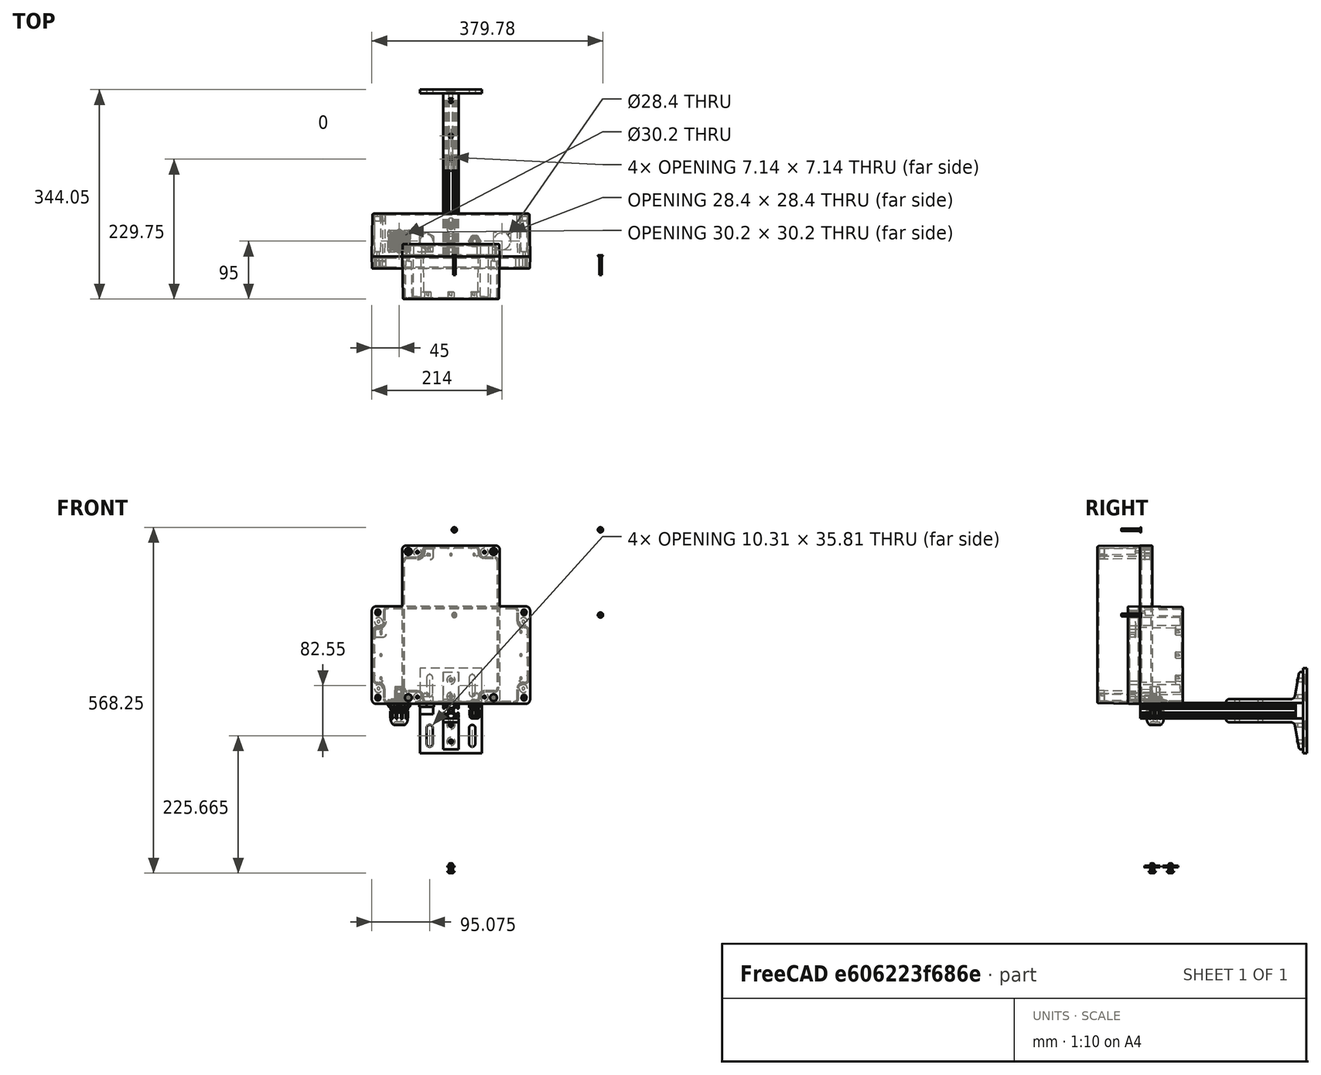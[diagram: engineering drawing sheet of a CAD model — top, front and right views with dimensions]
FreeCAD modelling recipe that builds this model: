
FCSTD DOCUMENT  (FreeCAD 0.20R29410 (Git))
Label: gateWayModuleTest
License: All rights reserved
LicenseURL: http://en.wikipedia.org/wiki/All_rights_reserved
objects: Part::Feature×42, TechDraw::DrawViewDimension×36, Part::Cylinder×28, Part::MultiFuse×9, App::Part×8, Part::Cut×4, TechDraw::DrawViewPart×4, TechDraw::DrawSVGTemplate×2, TechDraw::DrawPage×2, Part::Box×1, Sketcher::SketchObject×1, Part::Extrusion×1, TechDraw::DrawViewAnnotation×1
note: 86 computed .brp shape members not serialized (recipe doc carries the construction recipe); baked Part::Feature solids carry a one-line shape summary decoded from their .brp

FEATURE [Part::Feature] Part__Feature  label="AN-23B_AN-23BP-01"
  shape: bbox 160 x 71.5 x 260 mm, 302 faces (baked)
FEATURE [Part::Feature] Part__Feature001  label="AN-23C_AN-23C-01"
  shape: bbox 160.5 x 20 x 260.5 mm, 243 faces (baked)
FEATURE [Part::Feature] Part__Feature002  label="cross recessed countersunk head screw_jis_JIS 1111 Cross recessed countersunk head screw - M4 x 32 - Z --24CSST"
  Placement = pos=(245.578,1.4369,155.7) rot=(0.642635,-0.642635,0.417181;3.93205rad)
  shape: bbox 8.4 x 32 x 8.4 mm, 32 faces (baked)
FEATURE [Part::Feature] Part__Feature003  label="cross recessed countersunk head screw_jis_JIS 1111 Cross recessed countersunk head screw - M4 x 32 - Z --24CSST001"
  Placement = pos=(245.578,1.4369,15.6996) rot=(0.610522,-0.610522,0.504506;4.07608rad)
  shape: bbox 8.4 x 32 x 8.4 mm, 32 faces (baked)
FEATURE [Part::Feature] Part__Feature004  label="cross recessed countersunk head screw_jis_JIS 1111 Cross recessed countersunk head screw - M4 x 32 - Z --24CSST002"
  Placement = pos=(5.5776,1.4369,15.6996) rot=(0.641113,-0.641113,0.421839;3.93997rad)
  shape: bbox 8.4 x 32 x 8.4 mm, 32 faces (baked)
FEATURE [Part::Feature] Part__Feature005  label="cross recessed countersunk head screw_jis_JIS 1111 Cross recessed countersunk head screw - M4 x 32 - Z --24CSST003"
  Placement = pos=(5.5776,1.4369,155.7) rot=(0.666667,-0.666667,0.333333;3.78509rad)
  shape: bbox 8.4 x 32 x 8.4 mm, 32 faces (baked)
FEATURE [App::Part] SCREWS_036_4  label="SCREWS-036-4"
  Group = -> [Part__Feature002,Part__Feature003,Part__Feature004,Part__Feature005]
  Origin = -> Origin
  Placement = pos=(85.6996,18.1356,-125.578) rot=(0,-1,0;1.5708rad)
FEATURE [Part::Feature] Part__Feature006  label="GASKET-123-01"
  Placement = pos=(0,1.04,0) rot=(0,0,1;0rad)
  shape: bbox 157.7 x 1.5 x 257.7 mm, 98 faces (baked)
FEATURE [App::Part] AN_23P_01  label="AN-23P-01"
  Group = -> [Part__Feature,Part__Feature001,SCREWS_036_4,Part__Feature006]
  Origin = -> Origin001
  Placement = pos=(0,0,-50) rot=(0.707107,0,-0.707107;3.14159rad)
FEATURE [Part::Box] Box  label="Gateway"
  AttacherType = Attacher::AttachEngine3D
  Height = 120
  Length = 120
  Placement = pos=(-66,26,-100) rot=(0,0,1;0rad)
  Width = 30
FEATURE [Part::Cylinder] Cylinder030  label="loraAntenna"
  Angle = 360
  AttacherType = Attacher::AttachEngine3D
  FirstAngle = 0
  Height = 1390
  Radius = 13
  SecondAngle = 0
FEATURE [Part::Cylinder] Cylinder031  label="loraAntenna001"
  Angle = 360
  AttacherType = Attacher::AttachEngine3D
  FirstAngle = 0
  Height = 204
  Radius = 15
  SecondAngle = 0
FEATURE [Part::Cylinder] Cylinder032  label="loraAntenna002"
  Angle = 360
  AttacherType = Attacher::AttachEngine3D
  FirstAngle = 0
  Height = 27
  Placement = pos=(0,0,1363) rot=(0,0,1;0rad)
  Radius = 14
  SecondAngle = 0
FEATURE [Part::MultiFuse] Fusion006  label="loraAntenna003"
  Placement = pos=(0,0,188) rot=(0,0,1;0rad)
  Shapes = -> [Cylinder030,Cylinder032]
FEATURE [Part::MultiFuse] Fusion007  label="loraAntenna004"
  Placement = pos=(0,103,-127) rot=(0,0,1;0rad)
  Shapes = -> [Fusion006,Cylinder031]
FEATURE [Part::Feature] Part__Feature008  label="CUI_VGS-25W-5"
  Placement = pos=(-42,23,-27) rot=(1,0,0;3.14159rad)
  shape: bbox 55.36 x 25.53 x 90.37 mm, 2734 faces, 26 solids (baked)
FEATURE [Part::Feature] Part__Feature009  label="DCC-RJ6ST-310"
  Placement = pos=(-85,25,-123) rot=(0,0,1;0rad)
  shape: bbox 40.36 x 68.07 x 51.72 mm, 441 faces (baked)
FEATURE [Part::Feature] Part__Feature010  label="DCP-RJ6ST-F"
  Placement = pos=(-85,25,-123.5) rot=(0,1,0;3.14159rad)
  shape: bbox 40.26 x 40.33 x 38.85 mm, 485 faces, 2 solids (baked)
FEATURE [Part::Cylinder] Cylinder  label="plugIn"
  Angle = 360
  AttacherType = Attacher::AttachEngine3D
  FirstAngle = 0
  Height = 28.19
  Radius = 11
  SecondAngle = 0
FEATURE [Sketcher::SketchObject] Sketch
  FullyConstrained = true
  sketch-geometry (7):
    g0: LineSegment StartX=12.25 StartY=-7.07254 StartZ=0 EndX=12.25 EndY=7.07254 EndZ=0
    g1: LineSegment StartX=12.25 StartY=7.07254 StartZ=0 EndX=0 EndY=14.1451 EndZ=0
    g2: LineSegment StartX=0 StartY=14.1451 StartZ=0 EndX=-12.25 EndY=7.07254 EndZ=0
    g3: LineSegment StartX=-12.25 StartY=7.07254 StartZ=0 EndX=-12.25 EndY=-7.07254 EndZ=0
    g4: LineSegment StartX=-12.25 StartY=-7.07254 StartZ=0 EndX=0 EndY=-14.1451 EndZ=0
    g5: LineSegment StartX=0 StartY=-14.1451 StartZ=0 EndX=12.25 EndY=-7.07254 EndZ=0
    g6: Circle CenterX=0 CenterY=0 CenterZ=0 NormalX=0 NormalY=0 NormalZ=1 AngleXU=0 Radius=14.1451
  constraints (17):
    c: Coincident(g0,g1)
    c: Coincident(g1,g2)
    c: Coincident(g2,g3)
    c: Coincident(g3,g4)
    c: Coincident(g4,g5)
    c: Coincident(g5,g0)
    c: Equal(g0, g1-g5) x5
    c: PointOnObject(g0,g6)
    c: PointOnObject(g1,g6)
    c: PointOnObject(g2,g6)
    c: PointOnObject(g3,g6)
    c: PointOnObject(g4,g6)
    c: PointOnObject(g5,g6)
    c: DistanceY(g6) = 0
    c: DistanceX(g6) = 0
    c: DistanceX(g1) = 0
    c: DistanceX(g2,g0) = 24.5
FEATURE [Part::Extrusion] Extrude
  Base = -> Sketch
  Dir = (0,0,1)
  DirMode = 2
  FaceMakerClass = Part::FaceMakerBullseye
  LengthFwd = 4.83
  LengthRev = 0
  Placement = pos=(0,0,12.19) rot=(0,0,1;0rad)
  Solid = true
  Symmetric = false
FEATURE [Part::MultiFuse] Fusion  label="powerPlug"
  Placement = pos=(-40,25,-147) rot=(0,0,1;0rad)
  Shapes = -> [Cylinder,Extrude]
FEATURE [Part::Feature] Part__Feature021  label="LoRaAntennaGland"
  Placement = pos=(84,25,-120) rot=(-1,0,0;1.5708rad)
  shape: bbox 36.99 x 36.69 x 48.04 mm, 518 faces, 0 solids (baked)
FEATURE [Part::Feature] Part__Feature022  label="3136N138_T-Slotted Framing"
  Placement = pos=(0,200.3,0) rot=(0,0,1;0rad)
  shape: bbox 101.6 x 133.4 x 139.7 mm, 136 faces (baked)
FEATURE [Part::Feature] Part__Feature023  label="47065T801_T-Slotted Framing"
  Placement = pos=(0,288.5,0) rot=(-1,0,0;1.5708rad)
  shape: bbox 25.4 x 152.4 x 25.4 mm, 108 faces (baked)
FEATURE [Part::Feature] Part__Feature024  label="47065T801_T-Slotted Framing001"
  Placement = pos=(0,391.5,0) rot=(-1,0,0;1.5708rad)
  shape: bbox 25.4 x 152.4 x 25.4 mm, 108 faces (baked)
FEATURE [Part::MultiFuse] Fusion008  label="framingSupport"
  Placement = pos=(0,468,-141.41) rot=(0,0,1;3.14159rad)
  Shapes = -> [Part__Feature024,Part__Feature022,Part__Feature023]
FEATURE [Part::Feature] Part__Feature025  label="Cable Gland PG7-PG19 Body_PG008"
  shape: bbox 17.67 x 27.9 x 16 mm, 147 faces (baked)
FEATURE [Part::Feature] Part__Feature026  label="Cable Gland PG7-PG19 Washer_PG008"
  Placement = pos=(0,-2.8,0) rot=(0,0,1;0rad)
  shape: bbox 16.6 x 1.2 x 16.6 mm, 6 faces (baked)
FEATURE [Part::Feature] Part__Feature027  label="Cable Gland PG7-PG19 Lock Nut_PG008"
  Placement = pos=(0,-5.6,0) rot=(0,0,1;3.14159rad)
  shape: bbox 19.6 x 5.77 x 19.6 mm, 32 faces (baked)
FEATURE [Part::Feature] Part__Feature028  label="Cable Gland PG7-PG19 Sleeve_PG008"
  Placement = pos=(0,13.65,0) rot=(0,0,1;0rad)
  shape: bbox 8.4 x 6.7 x 8.4 mm, 6 faces (baked)
FEATURE [Part::Feature] Part__Feature029  label="Cable Gland PG7-PG19 Gland Nut_PG008"
  Placement = pos=(0,10.95,0) rot=(0,-1,0;1.94172rad)
  shape: bbox 16.87 x 14 x 16.87 mm, 64 faces (baked)
FEATURE [Part::MultiFuse] Fusion011  label="pg7-Copper"
  Placement = pos=(39,25,-134) rot=(-1,0,0;1.5708rad)
  Shapes = -> [Part__Feature025,Part__Feature026,Part__Feature027,Part__Feature028,Part__Feature029]
FEATURE [Part::Cylinder] Cylinder033  label="EthernetCut"
  Angle = 360
  AttacherType = Attacher::AttachEngine3D
  FirstAngle = 0
  Height = 50
  Placement = pos=(-85,25,-147) rot=(0,0,1;0rad)
  Radius = 15.1
  SecondAngle = 0
FEATURE [Part::Cylinder] Cylinder034  label="PowerCut"
  Angle = 360
  AttacherType = Attacher::AttachEngine3D
  FirstAngle = 0
  Height = 50
  Placement = pos=(-40,25,-147) rot=(0,0,1;0rad)
  Radius = 11
  SecondAngle = 0
FEATURE [Part::Cylinder] Cylinder035  label="pg7Cut"
  Angle = 360
  AttacherType = Attacher::AttachEngine3D
  FirstAngle = 0
  Height = 50
  Placement = pos=(39,25,-147) rot=(0,0,1;0rad)
  Radius = 6.4
  SecondAngle = 0
FEATURE [Part::Cylinder] Cylinder036  label="AnetnnaCut"
  Angle = 360
  AttacherType = Attacher::AttachEngine3D
  FirstAngle = 0
  Height = 50
  Placement = pos=(84,25,-147) rot=(0,0,1;0rad)
  Radius = 14.2
  SecondAngle = 0
FEATURE [Part::Feature] Part__Feature030  label="47065T139_T-Slotted Framing"
  Placement = pos=(0,20,-405) rot=(0.57735,0.57735,-0.57735;4.18879rad)
  shape: bbox 11.25 x 25.4 x 17.44 mm, 56 faces, 2 solids (baked)
FEATURE [Part::Feature] Part__Feature031  label="47065T139_T-Slotted Framing001"
  Placement = pos=(0,50,-405) rot=(0.57735,0.57735,-0.57735;4.18879rad)
  shape: bbox 11.25 x 25.4 x 17.44 mm, 56 faces, 2 solids (baked)
FEATURE [Part::Cylinder] Cylinder037  label="m5Cut"
  Angle = 360
  AttacherType = Attacher::AttachEngine3D
  FirstAngle = 0
  Height = 50
  Placement = pos=(0,20,-147) rot=(0,0,1;0rad)
  Radius = 3.2
  SecondAngle = 0
FEATURE [Part::Cylinder] Cylinder038  label="m5Cut001"
  Angle = 360
  AttacherType = Attacher::AttachEngine3D
  FirstAngle = 0
  Height = 50
  Placement = pos=(0,50,-147) rot=(0,0,1;0rad)
  Radius = 3.2
  SecondAngle = 0
FEATURE [Part::MultiFuse] Fusion012
  Shapes = -> [Cylinder038,Cylinder037,Cylinder036,Cylinder035,Cylinder033,Cylinder034]
FEATURE [Part::Cut] Cut
  Base = -> AN_23P_01
  Tool = -> Fusion012
FEATURE [TechDraw::DrawSVGTemplate] Template
  EditableTexts = Designed_by_Name=Lakitha Wijeratne; Drawing_number=V1; FC-Date=November 14th 2022; FC-SC=0.5; FC-Title=MINTS Gateway Module; Subtitle=Cutouts for Polycase AN-23P Black
  Height = 210
  Orientation = 1
  Width = 297
FEATURE [TechDraw::DrawViewPart] View  label="Internal View"
  CoarseView = false
  Direction = (0.577,-0.577,0.577)
  Focus = 100
  HardHidden = false
  IsoCount = 0
  IsoHidden = false
  IsoVisible = false
  LockPosition = false
  Perspective = false
  Rotation = 0
  Scale = 0.5
  ScaleType = 0
  SeamHidden = false
  SeamVisible = true
  SmoothHidden = false
  SmoothVisible = true
  Source = -> [Cut]
  X = 221.274
  XDirection = (0.707,0.707,0)
  Y = 135.96
FEATURE [TechDraw::DrawViewPart] View001  label="Bottom View"
  CoarseView = false
  Direction = (0,0,-1)
  Focus = 100
  HardHidden = false
  IsoCount = 0
  IsoHidden = false
  IsoVisible = false
  LockPosition = false
  Perspective = false
  Rotation = 0
  Scale = 0.5
  ScaleType = 0
  SeamHidden = false
  SeamVisible = true
  SmoothHidden = false
  SmoothVisible = true
  Source = -> [Cut]
  X = 84.2092
  XDirection = (1,0,0)
  Y = 168.275
FEATURE [Part::Cylinder] Cylinder039  label="EthernetCut001"
  Angle = 360
  AttacherType = Attacher::AttachEngine3D
  FirstAngle = 0
  Height = 50
  Placement = pos=(-85,25,-147) rot=(0,0,1;0rad)
  Radius = 15.1
  SecondAngle = 0
FEATURE [Part::Cylinder] Cylinder040  label="PowerCut001"
  Angle = 360
  AttacherType = Attacher::AttachEngine3D
  FirstAngle = 0
  Height = 50
  Placement = pos=(-40,25,-147) rot=(0,0,1;0rad)
  Radius = 11
  SecondAngle = 0
FEATURE [Part::Cylinder] Cylinder041  label="pg7Cut001"
  Angle = 360
  AttacherType = Attacher::AttachEngine3D
  FirstAngle = 0
  Height = 50
  Placement = pos=(39,25,-147) rot=(0,0,1;0rad)
  Radius = 6.4
  SecondAngle = 0
FEATURE [Part::Cylinder] Cylinder042  label="AnetnnaCut001"
  Angle = 360
  AttacherType = Attacher::AttachEngine3D
  FirstAngle = 0
  Height = 50
  Placement = pos=(84,25,-147) rot=(0,0,1;0rad)
  Radius = 14.2
  SecondAngle = 0
FEATURE [Part::Cylinder] Cylinder043  label="m5Cut002"
  Angle = 360
  AttacherType = Attacher::AttachEngine3D
  FirstAngle = 0
  Height = 50
  Placement = pos=(0,20,-147) rot=(0,0,1;0rad)
  Radius = 3.2
  SecondAngle = 0
FEATURE [Part::Cylinder] Cylinder044  label="m5Cut003"
  Angle = 360
  AttacherType = Attacher::AttachEngine3D
  FirstAngle = 0
  Height = 50
  Placement = pos=(0,50,-147) rot=(0,0,1;0rad)
  Radius = 3.2
  SecondAngle = 0
FEATURE [Part::MultiFuse] Fusion013
  Shapes = -> [Cylinder044,Cylinder043,Cylinder042,Cylinder041,Cylinder039,Cylinder040]
FEATURE [Part::Feature] Part__Feature032  label="AN-23B_AN-23BP-002"
  shape: bbox 160 x 71.5 x 260 mm, 302 faces (baked)
FEATURE [Part::Feature] Part__Feature033  label="AN-23C_AN-23C-002"
  shape: bbox 160.5 x 20 x 260.5 mm, 243 faces (baked)
FEATURE [Part::Feature] Part__Feature034  label="cross recessed countersunk head screw_jis_JIS 1111 Cross recessed countersunk head screw - M4 x 32 - Z --24CSST004"
  Placement = pos=(245.578,1.4369,155.7) rot=(0.642635,-0.642635,0.417181;3.93205rad)
  shape: bbox 8.4 x 32 x 8.4 mm, 32 faces (baked)
FEATURE [Part::Feature] Part__Feature035  label="cross recessed countersunk head screw_jis_JIS 1111 Cross recessed countersunk head screw - M4 x 32 - Z --24CSST005"
  Placement = pos=(245.578,1.4369,15.6996) rot=(0.610522,-0.610522,0.504506;4.07608rad)
  shape: bbox 8.4 x 32 x 8.4 mm, 32 faces (baked)
FEATURE [Part::Feature] Part__Feature036  label="cross recessed countersunk head screw_jis_JIS 1111 Cross recessed countersunk head screw - M4 x 32 - Z --24CSST006"
  Placement = pos=(5.5776,1.4369,15.6996) rot=(0.641113,-0.641113,0.421839;3.93997rad)
  shape: bbox 8.4 x 32 x 8.4 mm, 32 faces (baked)
FEATURE [Part::Feature] Part__Feature037  label="cross recessed countersunk head screw_jis_JIS 1111 Cross recessed countersunk head screw - M4 x 32 - Z --24CSST007"
  Placement = pos=(5.5776,1.4369,155.7) rot=(0.666667,-0.666667,0.333333;3.78509rad)
  shape: bbox 8.4 x 32 x 8.4 mm, 32 faces (baked)
FEATURE [Part::Feature] Part__Feature038  label="GASKET-123-002"
  Placement = pos=(0,1.04,0) rot=(0,0,1;0rad)
  shape: bbox 157.7 x 1.5 x 257.7 mm, 98 faces (baked)
FEATURE [App::Part] SCREWS_036_005  label="SCREWS-036-005"
  Group = -> [Part__Feature034,Part__Feature035,Part__Feature036,Part__Feature037]
  Origin = -> Origin002
  Placement = pos=(85.6996,18.1356,-125.578) rot=(0,-1,0;1.5708rad)
FEATURE [App::Part] AN_23P_002  label="AN-23P-002"
  Group = -> [Part__Feature032,Part__Feature033,SCREWS_036_005,Part__Feature038]
  Origin = -> Origin003
  Placement = pos=(0,0,-50) rot=(0.707107,0,-0.707107;3.14159rad)
FEATURE [Part::Cut] Cut001  label="totalView"
  Base = -> AN_23P_002
  Tool = -> Fusion013
FEATURE [TechDraw::DrawViewPart] View002  label="External View"
  CoarseView = false
  Direction = (0.673,-0.641,-0.369)
  Focus = 100
  HardHidden = false
  IsoCount = 0
  IsoHidden = false
  IsoVisible = false
  LockPosition = false
  Perspective = false
  Rotation = 0
  Scale = 0.5
  ScaleType = 0
  SeamHidden = false
  SeamVisible = true
  SmoothHidden = false
  SmoothVisible = true
  Source = -> [Cut001]
  X = 86.3288
  XDirection = (0.739,0.594,0.316)
  Y = 76.7663
FEATURE [TechDraw::DrawViewDimension] Dimension
  AngleOverride = false
  Arbitrary = false
  ArbitraryTolerances = false
  EqualTolerance = true
  ExtensionAngle = 0
  FormatSpec = ⌀%.2w
  FormatSpecOverTolerance = %+.2w
  FormatSpecUnderTolerance = %+.2w
  Inverted = false
  LineAngle = 0
  LockPosition = false
  MeasureType = 1
  OverTolerance = 0
  References2D = -> [View001]
  Rotation = 0
  Scale = 0.5
  ScaleType = 0
  TheoreticalExact = false
  Type = 5
  UnderTolerance = 0
  X = -54.3759
  Y = 16.2133
FEATURE [TechDraw::DrawViewDimension] Dimension001
  AngleOverride = false
  Arbitrary = false
  ArbitraryTolerances = false
  EqualTolerance = true
  ExtensionAngle = 0
  FormatSpec = ⌀%.2w
  FormatSpecOverTolerance = %+.2w
  FormatSpecUnderTolerance = %+.2w
  Inverted = false
  LineAngle = 0
  LockPosition = false
  MeasureType = 1
  OverTolerance = 0
  References2D = -> [View001]
  Rotation = 0
  Scale = 0.5
  ScaleType = 0
  TheoreticalExact = false
  Type = 5
  UnderTolerance = 0
  X = -24.7872
  Y = 16.2975
FEATURE [TechDraw::DrawViewDimension] Dimension002
  AngleOverride = false
  Arbitrary = false
  ArbitraryTolerances = false
  EqualTolerance = true
  ExtensionAngle = 0
  FormatSpec = ⌀%.2w
  FormatSpecOverTolerance = %+.2w
  FormatSpecUnderTolerance = %+.2w
  Inverted = false
  LineAngle = 0
  LockPosition = false
  MeasureType = 1
  OverTolerance = 0
  References2D = -> [View001]
  Rotation = 0
  Scale = 0.5
  ScaleType = 0
  TheoreticalExact = false
  Type = 5
  UnderTolerance = 0
  X = 5.16691
  Y = 14.3503
FEATURE [TechDraw::DrawViewDimension] Dimension003
  AngleOverride = false
  Arbitrary = false
  ArbitraryTolerances = false
  EqualTolerance = true
  ExtensionAngle = 0
  FormatSpec = ⌀%.2w
  FormatSpecOverTolerance = %+.2w
  FormatSpecUnderTolerance = %+.2w
  Inverted = false
  LineAngle = 0
  LockPosition = false
  MeasureType = 1
  OverTolerance = 0
  References2D = -> [View001]
  Rotation = 0
  Scale = 0.5
  ScaleType = 0
  TheoreticalExact = false
  Type = 5
  UnderTolerance = 0
  X = 6.79278
  Y = 3.20489
FEATURE [TechDraw::DrawViewDimension] Dimension004
  AngleOverride = false
  Arbitrary = false
  ArbitraryTolerances = false
  EqualTolerance = true
  ExtensionAngle = 0
  FormatSpec = ⌀%.2w
  FormatSpecOverTolerance = %+.2w
  FormatSpecUnderTolerance = %+.2w
  Inverted = false
  LineAngle = 0
  LockPosition = false
  MeasureType = 1
  OverTolerance = 0
  References2D = -> [View001]
  Rotation = 0
  Scale = 0.5
  ScaleType = 0
  TheoreticalExact = false
  Type = 5
  UnderTolerance = 0
  X = 25.1396
  Y = 14.8713
FEATURE [TechDraw::DrawViewDimension] Dimension005
  AngleOverride = false
  Arbitrary = false
  ArbitraryTolerances = false
  EqualTolerance = true
  ExtensionAngle = 0
  FormatSpec = ⌀%.2w
  FormatSpecOverTolerance = %+.2w
  FormatSpecUnderTolerance = %+.2w
  Inverted = false
  LineAngle = 0
  LockPosition = false
  MeasureType = 1
  OverTolerance = 0
  References2D = -> [View001]
  Rotation = 0
  Scale = 0.5
  ScaleType = 0
  TheoreticalExact = false
  Type = 5
  UnderTolerance = 0
  X = 53.9059
  Y = 15.1805
FEATURE [TechDraw::DrawViewDimension] Dimension006
  AngleOverride = false
  Arbitrary = false
  ArbitraryTolerances = false
  EqualTolerance = true
  ExtensionAngle = 0
  FormatSpec = %.2w
  FormatSpecOverTolerance = %+.2w
  FormatSpecUnderTolerance = %+.2w
  Inverted = false
  LineAngle = 0
  LockPosition = false
  MeasureType = 1
  OverTolerance = 0
  References2D = -> [View001]
  Rotation = 0
  Scale = 0.5
  ScaleType = 0
  TheoreticalExact = false
  Type = 1
  UnderTolerance = 0
  X = -53.7744
  Y = -18.6501
FEATURE [TechDraw::DrawViewDimension] Dimension007
  AngleOverride = false
  Arbitrary = false
  ArbitraryTolerances = false
  EqualTolerance = true
  ExtensionAngle = 0
  FormatSpec = %.2w
  FormatSpecOverTolerance = %+.2w
  FormatSpecUnderTolerance = %+.2w
  Inverted = false
  LineAngle = 0
  LockPosition = false
  MeasureType = 1
  OverTolerance = 0
  References2D = -> [View001]
  Rotation = 0
  Scale = 0.5
  ScaleType = 0
  TheoreticalExact = false
  Type = 1
  UnderTolerance = 0
  X = -35.7058
  Y = -24.4298
FEATURE [TechDraw::DrawViewDimension] Dimension009
  AngleOverride = false
  Arbitrary = false
  ArbitraryTolerances = false
  EqualTolerance = true
  ExtensionAngle = 0
  FormatSpec = %.2w
  FormatSpecOverTolerance = %+.2w
  FormatSpecUnderTolerance = %+.2w
  Inverted = false
  LineAngle = 0
  LockPosition = false
  MeasureType = 1
  OverTolerance = 0
  References2D = -> [View001]
  Rotation = 0
  Scale = 0.5
  ScaleType = 0
  TheoreticalExact = false
  Type = 1
  UnderTolerance = 0
  X = -39.2827
  Y = -33.1748
FEATURE [TechDraw::DrawViewDimension] Dimension010
  AngleOverride = false
  Arbitrary = false
  ArbitraryTolerances = false
  EqualTolerance = true
  ExtensionAngle = 0
  FormatSpec = %.2w
  FormatSpecOverTolerance = %+.2w
  FormatSpecUnderTolerance = %+.2w
  Inverted = false
  LineAngle = 0
  LockPosition = false
  MeasureType = 1
  OverTolerance = 0
  References2D = -> [View001]
  Rotation = 0
  Scale = 0.5
  ScaleType = 0
  TheoreticalExact = false
  Type = 1
  UnderTolerance = 0
  X = 47.8554
  Y = -25.9182
FEATURE [TechDraw::DrawViewDimension] Dimension011
  AngleOverride = false
  Arbitrary = false
  ArbitraryTolerances = false
  EqualTolerance = true
  ExtensionAngle = 0
  FormatSpec = %.2w
  FormatSpecOverTolerance = %+.2w
  FormatSpecUnderTolerance = %+.2w
  Inverted = false
  LineAngle = 0
  LockPosition = false
  MeasureType = 1
  OverTolerance = 0
  References2D = -> [View001]
  Rotation = 0
  Scale = 0.5
  ScaleType = 0
  TheoreticalExact = false
  Type = 1
  UnderTolerance = 0
  X = 54.1367
  Y = -18.5094
FEATURE [TechDraw::DrawViewDimension] Dimension012
  AngleOverride = false
  Arbitrary = false
  ArbitraryTolerances = false
  EqualTolerance = true
  ExtensionAngle = 0
  FormatSpec = %.2w
  FormatSpecOverTolerance = %+.2w
  FormatSpecUnderTolerance = %+.2w
  Inverted = false
  LineAngle = 0
  LockPosition = false
  MeasureType = 1
  OverTolerance = 0
  References2D = -> [View001]
  Rotation = 0
  Scale = 0.5
  ScaleType = 0
  TheoreticalExact = false
  Type = 2
  UnderTolerance = 0
  X = -36.989
  Y = 15.3034
FEATURE [TechDraw::DrawViewDimension] Dimension013
  AngleOverride = false
  Arbitrary = false
  ArbitraryTolerances = false
  EqualTolerance = true
  ExtensionAngle = 0
  FormatSpec = %.2w
  FormatSpecOverTolerance = %+.2w
  FormatSpecUnderTolerance = %+.2w
  Inverted = false
  LineAngle = 0
  LockPosition = false
  MeasureType = 1
  OverTolerance = 0
  References2D = -> [View001]
  Rotation = 0
  Scale = 0.5
  ScaleType = 0
  TheoreticalExact = false
  Type = 1
  UnderTolerance = 0
  X = -29.3162
  Y = 29.8128
FEATURE [TechDraw::DrawViewDimension] Dimension014
  AngleOverride = false
  Arbitrary = false
  ArbitraryTolerances = false
  EqualTolerance = true
  ExtensionAngle = 0
  FormatSpec = %.2w
  FormatSpecOverTolerance = %+.2w
  FormatSpecUnderTolerance = %+.2w
  Inverted = false
  LineAngle = 0
  LockPosition = false
  MeasureType = 1
  OverTolerance = 0
  References2D = -> [View001]
  Rotation = 0
  Scale = 0.5
  ScaleType = 0
  TheoreticalExact = false
  Type = 2
  UnderTolerance = 0
  X = 14.9293
  Y = 13.6113
FEATURE [TechDraw::DrawViewDimension] Dimension015
  AngleOverride = false
  Arbitrary = false
  ArbitraryTolerances = false
  EqualTolerance = true
  ExtensionAngle = 0
  FormatSpec = %.2w
  FormatSpecOverTolerance = %+.2w
  FormatSpecUnderTolerance = %+.2w
  Inverted = false
  LineAngle = 0
  LockPosition = false
  MeasureType = 1
  OverTolerance = 0
  References2D = -> [View001]
  Rotation = 0
  Scale = 0.5
  ScaleType = 0
  TheoreticalExact = false
  Type = 2
  UnderTolerance = 0
  X = 34.9847
  Y = 13.4844
FEATURE [TechDraw::DrawViewAnnotation] Annotation
  Font = osifont
  LineSpace = 80
  LockPosition = false
  MaxWidth = -1
  Rotation = 0
  Scale = 0.5
  ScaleType = 0
  Text = MINTS Artwork
  TextSize = 5
  TextStyle = 0
  X = 74.9972
  Y = 88.0198
FEATURE [TechDraw::DrawViewDimension] Dimension016
  AngleOverride = false
  Arbitrary = false
  ArbitraryTolerances = false
  EqualTolerance = true
  ExtensionAngle = 0
  FormatSpec = %.2w
  FormatSpecOverTolerance = %+.2w
  FormatSpecUnderTolerance = %+.2w
  Inverted = false
  LineAngle = 0
  LockPosition = false
  MeasureType = 1
  OverTolerance = 0
  References2D = -> [View001]
  Rotation = 0
  Scale = 0.5
  ScaleType = 0
  TheoreticalExact = false
  Type = 2
  UnderTolerance = 0
  X = -4.81759
  Y = 14.1292
FEATURE [TechDraw::DrawViewDimension] Dimension017
  AngleOverride = false
  Arbitrary = false
  ArbitraryTolerances = false
  EqualTolerance = true
  ExtensionAngle = 0
  FormatSpec = %.2w
  FormatSpecOverTolerance = %+.2w
  FormatSpecUnderTolerance = %+.2w
  Inverted = false
  LineAngle = 0
  LockPosition = false
  MeasureType = 1
  OverTolerance = 0
  References2D = -> [View001]
  Rotation = 0
  Scale = 0.5
  ScaleType = 0
  TheoreticalExact = false
  Type = 2
  UnderTolerance = 0
  X = -10.0786
  Y = 5.19442
FEATURE [TechDraw::DrawViewDimension] Dimension018
  AngleOverride = false
  Arbitrary = false
  ArbitraryTolerances = false
  EqualTolerance = true
  ExtensionAngle = 0
  FormatSpec = %.2w
  FormatSpecOverTolerance = %+.2w
  FormatSpecUnderTolerance = %+.2w
  Inverted = false
  LineAngle = 0
  LockPosition = false
  MeasureType = 1
  OverTolerance = 0
  References2D = -> [View001]
  Rotation = 0
  Scale = 0.5
  ScaleType = 0
  TheoreticalExact = false
  Type = 2
  UnderTolerance = 0
  X = -16.9958
  Y = 14.4097
FEATURE [TechDraw::DrawPage] Page
  KeepUpdated = true
  NextBalloonIndex = 1
  ProjectionType = 0
  Scale = 0.5
  Template = -> Template
  Views = -> [View,View001,View002,Dimension,Dimension001,Dimension002,Dimension003,Dimension004,Dimension005,Dimension006,Dimension007,Dimension009,Dimension010,Dimension011,Dimension012,Dimension013,Dimension014,Dimension015,Annotation,Dimension016,Dimension017,Dimension018]
FEATURE [Part::Cylinder] Cylinder045  label="EthernetCut002"
  Angle = 360
  AttacherType = Attacher::AttachEngine3D
  FirstAngle = 0
  Height = 50
  Placement = pos=(-85,25,-147) rot=(0,0,1;0rad)
  Radius = 15.1
  SecondAngle = 0
FEATURE [Part::Cylinder] Cylinder046  label="PowerCut002"
  Angle = 360
  AttacherType = Attacher::AttachEngine3D
  FirstAngle = 0
  Height = 50
  Placement = pos=(-40,25,-147) rot=(0,0,1;0rad)
  Radius = 11
  SecondAngle = 0
FEATURE [Part::Cylinder] Cylinder047  label="pg7Cut002"
  Angle = 360
  AttacherType = Attacher::AttachEngine3D
  FirstAngle = 0
  Height = 50
  Placement = pos=(39,25,-147) rot=(0,0,1;0rad)
  Radius = 6.4
  SecondAngle = 0
FEATURE [Part::Cylinder] Cylinder048  label="AnetnnaCut002"
  Angle = 360
  AttacherType = Attacher::AttachEngine3D
  FirstAngle = 0
  Height = 50
  Placement = pos=(84,25,-147) rot=(0,0,1;0rad)
  Radius = 14.2
  SecondAngle = 0
FEATURE [Part::Cylinder] Cylinder049  label="m5Cut004"
  Angle = 360
  AttacherType = Attacher::AttachEngine3D
  FirstAngle = 0
  Height = 50
  Placement = pos=(0,20,-147) rot=(0,0,1;0rad)
  Radius = 3.2
  SecondAngle = 0
FEATURE [Part::Cylinder] Cylinder050  label="m5Cut005"
  Angle = 360
  AttacherType = Attacher::AttachEngine3D
  FirstAngle = 0
  Height = 50
  Placement = pos=(0,50,-147) rot=(0,0,1;0rad)
  Radius = 3.2
  SecondAngle = 0
FEATURE [Part::Cylinder] Cylinder051  label="EthernetCut003"
  Angle = 360
  AttacherType = Attacher::AttachEngine3D
  FirstAngle = 0
  Height = 50
  Placement = pos=(-85,25,-147) rot=(0,0,1;0rad)
  Radius = 15.1
  SecondAngle = 0
FEATURE [Part::Cylinder] Cylinder052  label="PowerCut003"
  Angle = 360
  AttacherType = Attacher::AttachEngine3D
  FirstAngle = 0
  Height = 50
  Placement = pos=(-40,25,-147) rot=(0,0,1;0rad)
  Radius = 11
  SecondAngle = 0
FEATURE [Part::Cylinder] Cylinder053  label="pg7Cut003"
  Angle = 360
  AttacherType = Attacher::AttachEngine3D
  FirstAngle = 0
  Height = 50
  Placement = pos=(39,25,-147) rot=(0,0,1;0rad)
  Radius = 6.4
  SecondAngle = 0
FEATURE [Part::Cylinder] Cylinder054  label="AnetnnaCut003"
  Angle = 360
  AttacherType = Attacher::AttachEngine3D
  FirstAngle = 0
  Height = 50
  Placement = pos=(84,25,-147) rot=(0,0,1;0rad)
  Radius = 14.2
  SecondAngle = 0
FEATURE [Part::Cylinder] Cylinder055  label="m5Cut006"
  Angle = 360
  AttacherType = Attacher::AttachEngine3D
  FirstAngle = 0
  Height = 50
  Placement = pos=(0,20,-147) rot=(0,0,1;0rad)
  Radius = 3.2
  SecondAngle = 0
FEATURE [Part::Cylinder] Cylinder056  label="m5Cut007"
  Angle = 360
  AttacherType = Attacher::AttachEngine3D
  FirstAngle = 0
  Height = 50
  Placement = pos=(0,50,-147) rot=(0,0,1;0rad)
  Radius = 3.2
  SecondAngle = 0
FEATURE [Part::MultiFuse] Fusion014
  Shapes = -> [Cylinder050,Cylinder049,Cylinder048,Cylinder047,Cylinder045,Cylinder046]
FEATURE [Part::MultiFuse] Fusion015
  Shapes = -> [Cylinder056,Cylinder055,Cylinder054,Cylinder053,Cylinder051,Cylinder052]
FEATURE [Part::Feature] Part__Feature039  label="AN-23B_AN-23BP-003"
  shape: bbox 160 x 71.5 x 260 mm, 302 faces (baked)
FEATURE [Part::Feature] Part__Feature040  label="AN-23C_AN-23C-003"
  shape: bbox 160.5 x 20 x 260.5 mm, 243 faces (baked)
FEATURE [Part::Feature] Part__Feature041  label="cross recessed countersunk head screw_jis_JIS 1111 Cross recessed countersunk head screw - M4 x 32 - Z --24CSST008"
  Placement = pos=(245.578,1.4369,155.7) rot=(0.642635,-0.642635,0.417181;3.93205rad)
  shape: bbox 8.4 x 32 x 8.4 mm, 32 faces (baked)
FEATURE [Part::Feature] Part__Feature042  label="cross recessed countersunk head screw_jis_JIS 1111 Cross recessed countersunk head screw - M4 x 32 - Z --24CSST009"
  Placement = pos=(245.578,1.4369,15.6996) rot=(0.610522,-0.610522,0.504506;4.07608rad)
  shape: bbox 8.4 x 32 x 8.4 mm, 32 faces (baked)
FEATURE [Part::Feature] Part__Feature043  label="cross recessed countersunk head screw_jis_JIS 1111 Cross recessed countersunk head screw - M4 x 32 - Z --24CSST010"
  Placement = pos=(5.5776,1.4369,15.6996) rot=(0.641113,-0.641113,0.421839;3.93997rad)
  shape: bbox 8.4 x 32 x 8.4 mm, 32 faces (baked)
FEATURE [Part::Feature] Part__Feature044  label="cross recessed countersunk head screw_jis_JIS 1111 Cross recessed countersunk head screw - M4 x 32 - Z --24CSST011"
  Placement = pos=(5.5776,1.4369,155.7) rot=(0.666667,-0.666667,0.333333;3.78509rad)
  shape: bbox 8.4 x 32 x 8.4 mm, 32 faces (baked)
FEATURE [Part::Feature] Part__Feature045  label="GASKET-123-003"
  Placement = pos=(0,1.04,0) rot=(0,0,1;0rad)
  shape: bbox 157.7 x 1.5 x 257.7 mm, 98 faces (baked)
FEATURE [Part::Feature] Part__Feature046  label="AN-23B_AN-23BP-004"
  shape: bbox 160 x 71.5 x 260 mm, 302 faces (baked)
FEATURE [Part::Feature] Part__Feature047  label="AN-23C_AN-23C-004"
  shape: bbox 160.5 x 20 x 260.5 mm, 243 faces (baked)
FEATURE [Part::Feature] Part__Feature048  label="cross recessed countersunk head screw_jis_JIS 1111 Cross recessed countersunk head screw - M4 x 32 - Z --24CSST012"
  Placement = pos=(245.578,1.4369,155.7) rot=(0.642635,-0.642635,0.417181;3.93205rad)
  shape: bbox 8.4 x 32 x 8.4 mm, 32 faces (baked)
FEATURE [Part::Feature] Part__Feature049  label="cross recessed countersunk head screw_jis_JIS 1111 Cross recessed countersunk head screw - M4 x 32 - Z --24CSST013"
  Placement = pos=(245.578,1.4369,15.6996) rot=(0.610522,-0.610522,0.504506;4.07608rad)
  shape: bbox 8.4 x 32 x 8.4 mm, 32 faces (baked)
FEATURE [Part::Feature] Part__Feature050  label="cross recessed countersunk head screw_jis_JIS 1111 Cross recessed countersunk head screw - M4 x 32 - Z --24CSST014"
  Placement = pos=(5.5776,1.4369,15.6996) rot=(0.641113,-0.641113,0.421839;3.93997rad)
  shape: bbox 8.4 x 32 x 8.4 mm, 32 faces (baked)
FEATURE [Part::Feature] Part__Feature051  label="cross recessed countersunk head screw_jis_JIS 1111 Cross recessed countersunk head screw - M4 x 32 - Z --24CSST015"
  Placement = pos=(5.5776,1.4369,155.7) rot=(0.666667,-0.666667,0.333333;3.78509rad)
  shape: bbox 8.4 x 32 x 8.4 mm, 32 faces (baked)
FEATURE [Part::Feature] Part__Feature052  label="GASKET-123-004"
  Placement = pos=(0,1.04,0) rot=(0,0,1;0rad)
  shape: bbox 157.7 x 1.5 x 257.7 mm, 98 faces (baked)
FEATURE [App::Part] SCREWS_036_006  label="SCREWS-036-006"
  Group = -> [Part__Feature048,Part__Feature049,Part__Feature050,Part__Feature051]
  Origin = -> Origin006
  Placement = pos=(85.6996,18.1356,-125.578) rot=(0,-1,0;1.5708rad)
FEATURE [App::Part] AN_23P_003  label="AN-23P-003"
  Group = -> [Part__Feature046,Part__Feature047,SCREWS_036_006,Part__Feature052]
  Origin = -> Origin007
  Placement = pos=(0,0,-50) rot=(0.707107,0,-0.707107;3.14159rad)
FEATURE [Part::Cut] Cut003  label="totalView001"
  Base = -> AN_23P_003
  Tool = -> Fusion015
FEATURE [App::Part] SCREWS_036_007  label="SCREWS-036-007"
  Group = -> [Part__Feature041,Part__Feature042,Part__Feature043,Part__Feature044]
  Origin = -> Origin004
  Placement = pos=(85.6996,18.1356,-125.578) rot=(0,-1,0;1.5708rad)
FEATURE [App::Part] AN_23P_004  label="AN-23P-004"
  Group = -> [Part__Feature039,Part__Feature040,SCREWS_036_007,Part__Feature045]
  Origin = -> Origin005
  Placement = pos=(0,0,-50) rot=(0.707107,0,-0.707107;3.14159rad)
FEATURE [Part::Cut] Cut002
  Base = -> AN_23P_004
  Tool = -> Fusion014
FEATURE [TechDraw::DrawSVGTemplate] Template001
  EditableTexts = Designed_by_Name=Lakitha Wijeratne; Drawing_number=V1 - Bottom View; FC-Date=November 14th 2022; FC-SC=0.5; FC-Title=MINTS Gateway Module; Subtitle=Cutouts for Polycase AN-23P Black
  Height = 210
  Orientation = 1
  Width = 297
FEATURE [TechDraw::DrawViewPart] View004  label="Bottom View (Only)"
  CoarseView = false
  Direction = (0,0,-1)
  Focus = 100
  HardHidden = false
  IsoCount = 0
  IsoHidden = false
  IsoVisible = false
  LockPosition = false
  Perspective = false
  Rotation = 0
  ScaleType = 0
  SeamHidden = false
  SeamVisible = true
  SmoothHidden = false
  SmoothVisible = true
  Source = -> [Cut002]
  X = 148.914
  XDirection = (1,0,0)
  Y = 126.658
FEATURE [TechDraw::DrawViewDimension] Dimension019
  AngleOverride = false
  Arbitrary = false
  ArbitraryTolerances = false
  EqualTolerance = true
  ExtensionAngle = 0
  FormatSpec = ⌀%.2w
  FormatSpecOverTolerance = %+.2w
  FormatSpecUnderTolerance = %+.2w
  Inverted = false
  LineAngle = 0
  LockPosition = false
  MeasureType = 1
  OverTolerance = 0
  References2D = -> [View004]
  Rotation = 0
  ScaleType = 0
  TheoreticalExact = false
  Type = 5
  UnderTolerance = 0
  X = -79.9713
  Y = 18.1822
FEATURE [TechDraw::DrawViewDimension] Dimension020
  AngleOverride = false
  Arbitrary = false
  ArbitraryTolerances = false
  EqualTolerance = true
  ExtensionAngle = 0
  FormatSpec = ⌀%.2w
  FormatSpecOverTolerance = %+.2w
  FormatSpecUnderTolerance = %+.2w
  Inverted = false
  LineAngle = 0
  LockPosition = false
  MeasureType = 1
  OverTolerance = 0
  References2D = -> [View004]
  Rotation = 0
  ScaleType = 0
  TheoreticalExact = false
  Type = 5
  UnderTolerance = 0
  X = -35.8621
  Y = 16.7897
FEATURE [TechDraw::DrawViewDimension] Dimension021
  AngleOverride = false
  Arbitrary = false
  ArbitraryTolerances = false
  EqualTolerance = true
  ExtensionAngle = 0
  FormatSpec = ⌀%.2w
  FormatSpecOverTolerance = %+.2w
  FormatSpecUnderTolerance = %+.2w
  Inverted = false
  LineAngle = 0
  LockPosition = false
  MeasureType = 1
  OverTolerance = 0
  References2D = -> [View004]
  Rotation = 0
  ScaleType = 0
  TheoreticalExact = false
  Type = 5
  UnderTolerance = 0
  X = 5.16691
  Y = 28.6246
FEATURE [TechDraw::DrawViewDimension] Dimension022
  AngleOverride = false
  Arbitrary = false
  ArbitraryTolerances = false
  EqualTolerance = true
  ExtensionAngle = 0
  FormatSpec = ⌀%.2w
  FormatSpecOverTolerance = %+.2w
  FormatSpecUnderTolerance = %+.2w
  Inverted = false
  LineAngle = 0
  LockPosition = false
  MeasureType = 1
  OverTolerance = 0
  References2D = -> [View004]
  Rotation = 0
  ScaleType = 0
  TheoreticalExact = false
  Type = 5
  UnderTolerance = 0
  X = 7.77722
  Y = -3.93228
FEATURE [TechDraw::DrawViewDimension] Dimension023
  AngleOverride = false
  Arbitrary = false
  ArbitraryTolerances = false
  EqualTolerance = true
  ExtensionAngle = 0
  FormatSpec = ⌀%.2w
  FormatSpecOverTolerance = %+.2w
  FormatSpecUnderTolerance = %+.2w
  Inverted = false
  LineAngle = 0
  LockPosition = false
  MeasureType = 1
  OverTolerance = 0
  References2D = -> [View004]
  Rotation = 0
  ScaleType = 0
  TheoreticalExact = false
  Type = 5
  UnderTolerance = 0
  X = 52.95
  Y = 26.1923
FEATURE [TechDraw::DrawViewDimension] Dimension024
  AngleOverride = false
  Arbitrary = false
  ArbitraryTolerances = false
  EqualTolerance = true
  ExtensionAngle = 0
  FormatSpec = ⌀%.2w
  FormatSpecOverTolerance = %+.2w
  FormatSpecUnderTolerance = %+.2w
  Inverted = false
  LineAngle = 0
  LockPosition = false
  MeasureType = 1
  OverTolerance = 0
  References2D = -> [View004]
  Rotation = 0
  ScaleType = 0
  TheoreticalExact = false
  Type = 5
  UnderTolerance = 0
  X = 89.0995
  Y = 16.9032
FEATURE [TechDraw::DrawViewDimension] Dimension025
  AngleOverride = false
  Arbitrary = false
  ArbitraryTolerances = false
  EqualTolerance = true
  ExtensionAngle = 0
  FormatSpec = %.2w
  FormatSpecOverTolerance = %+.2w
  FormatSpecUnderTolerance = %+.2w
  Inverted = false
  LineAngle = 0
  LockPosition = false
  MeasureType = 1
  OverTolerance = 0
  References2D = -> [View004]
  Rotation = 0
  ScaleType = 0
  TheoreticalExact = false
  Type = 1
  UnderTolerance = 0
  X = -104.965
  Y = -7.57519
FEATURE [TechDraw::DrawViewDimension] Dimension026
  AngleOverride = false
  Arbitrary = false
  ArbitraryTolerances = false
  EqualTolerance = true
  ExtensionAngle = 0
  FormatSpec = %.2w
  FormatSpecOverTolerance = %+.2w
  FormatSpecUnderTolerance = %+.2w
  Inverted = false
  LineAngle = 0
  LockPosition = false
  MeasureType = 1
  OverTolerance = 0
  References2D = -> [View004]
  Rotation = 0
  ScaleType = 0
  TheoreticalExact = false
  Type = 1
  UnderTolerance = 0
  X = -63.7623
  Y = -9.66322
FEATURE [TechDraw::DrawViewDimension] Dimension027
  AngleOverride = false
  Arbitrary = false
  ArbitraryTolerances = false
  EqualTolerance = true
  ExtensionAngle = 0
  FormatSpec = %.2w
  FormatSpecOverTolerance = %+.2w
  FormatSpecUnderTolerance = %+.2w
  Inverted = false
  LineAngle = 0
  LockPosition = false
  MeasureType = 1
  OverTolerance = 0
  References2D = -> [View004]
  Rotation = 0
  ScaleType = 0
  TheoreticalExact = false
  Type = 1
  UnderTolerance = 0
  X = -63.6475
  Y = -23.3304
FEATURE [TechDraw::DrawViewDimension] Dimension028
  AngleOverride = false
  Arbitrary = false
  ArbitraryTolerances = false
  EqualTolerance = true
  ExtensionAngle = 0
  FormatSpec = %.2w
  FormatSpecOverTolerance = %+.2w
  FormatSpecUnderTolerance = %+.2w
  Inverted = false
  LineAngle = 0
  LockPosition = false
  MeasureType = 1
  OverTolerance = 0
  References2D = -> [View004]
  Rotation = 0
  ScaleType = 0
  TheoreticalExact = false
  Type = 1
  UnderTolerance = 0
  X = 98.0616
  Y = -20.7499
FEATURE [TechDraw::DrawViewDimension] Dimension029
  AngleOverride = false
  Arbitrary = false
  ArbitraryTolerances = false
  EqualTolerance = true
  ExtensionAngle = 0
  FormatSpec = %.2w
  FormatSpecOverTolerance = %+.2w
  FormatSpecUnderTolerance = %+.2w
  Inverted = false
  LineAngle = 0
  LockPosition = false
  MeasureType = 1
  OverTolerance = 0
  References2D = -> [View004]
  Rotation = 0
  ScaleType = 0
  TheoreticalExact = false
  Type = 1
  UnderTolerance = 0
  X = 106.312
  Y = -8.66499
FEATURE [TechDraw::DrawViewDimension] Dimension030
  AngleOverride = false
  Arbitrary = false
  ArbitraryTolerances = false
  EqualTolerance = true
  ExtensionAngle = 0
  FormatSpec = %.2w
  FormatSpecOverTolerance = %+.2w
  FormatSpecUnderTolerance = %+.2w
  Inverted = false
  LineAngle = 0
  LockPosition = false
  MeasureType = 1
  OverTolerance = 0
  References2D = -> [View004]
  Rotation = 0
  ScaleType = 0
  TheoreticalExact = false
  Type = 2
  UnderTolerance = 0
  X = -110.822
  Y = 26.8705
FEATURE [TechDraw::DrawViewDimension] Dimension031
  AngleOverride = false
  Arbitrary = false
  ArbitraryTolerances = false
  EqualTolerance = true
  ExtensionAngle = 0
  FormatSpec = %.2w
  FormatSpecOverTolerance = %+.2w
  FormatSpecUnderTolerance = %+.2w
  Inverted = false
  LineAngle = 0
  LockPosition = false
  MeasureType = 1
  OverTolerance = 0
  References2D = -> [View004]
  Rotation = 0
  ScaleType = 0
  TheoreticalExact = false
  Type = 1
  UnderTolerance = 0
  X = -68.4476
  Y = 54.6698
FEATURE [TechDraw::DrawViewDimension] Dimension032
  AngleOverride = false
  Arbitrary = false
  ArbitraryTolerances = false
  EqualTolerance = true
  ExtensionAngle = 0
  FormatSpec = %.2w
  FormatSpecOverTolerance = %+.2w
  FormatSpecUnderTolerance = %+.2w
  Inverted = false
  LineAngle = 0
  LockPosition = false
  MeasureType = 1
  OverTolerance = 0
  References2D = -> [View004]
  Rotation = 0
  ScaleType = 0
  TheoreticalExact = false
  Type = 2
  UnderTolerance = 0
  X = 15.4215
  Y = 20.9946
FEATURE [TechDraw::DrawViewDimension] Dimension033
  AngleOverride = false
  Arbitrary = false
  ArbitraryTolerances = false
  EqualTolerance = true
  ExtensionAngle = 0
  FormatSpec = %.2w
  FormatSpecOverTolerance = %+.2w
  FormatSpecUnderTolerance = %+.2w
  Inverted = false
  LineAngle = 0
  LockPosition = false
  MeasureType = 1
  OverTolerance = 0
  References2D = -> [View004]
  Rotation = 0
  ScaleType = 0
  TheoreticalExact = false
  Type = 2
  UnderTolerance = 0
  X = 27.3553
  Y = 23.3288
FEATURE [TechDraw::DrawViewDimension] Dimension034
  AngleOverride = false
  Arbitrary = false
  ArbitraryTolerances = false
  EqualTolerance = true
  ExtensionAngle = 0
  FormatSpec = %.2w
  FormatSpecOverTolerance = %+.2w
  FormatSpecUnderTolerance = %+.2w
  Inverted = false
  LineAngle = 0
  LockPosition = false
  MeasureType = 1
  OverTolerance = 0
  References2D = -> [View004]
  Rotation = 0
  ScaleType = 0
  TheoreticalExact = false
  Type = 2
  UnderTolerance = 0
  X = -9.24755
  Y = 25.9425
FEATURE [TechDraw::DrawViewDimension] Dimension035
  AngleOverride = false
  Arbitrary = false
  ArbitraryTolerances = false
  EqualTolerance = true
  ExtensionAngle = 0
  FormatSpec = %.2w
  FormatSpecOverTolerance = %+.2w
  FormatSpecUnderTolerance = %+.2w
  Inverted = false
  LineAngle = 0
  LockPosition = false
  MeasureType = 1
  OverTolerance = 0
  References2D = -> [View004]
  Rotation = 0
  ScaleType = 0
  TheoreticalExact = false
  Type = 2
  UnderTolerance = 0
  X = -18.9385
  Y = 1.74889
FEATURE [TechDraw::DrawViewDimension] Dimension036
  AngleOverride = false
  Arbitrary = false
  ArbitraryTolerances = false
  EqualTolerance = true
  ExtensionAngle = 0
  FormatSpec = %.2w
  FormatSpecOverTolerance = %+.2w
  FormatSpecUnderTolerance = %+.2w
  Inverted = false
  LineAngle = 0
  LockPosition = false
  MeasureType = 1
  OverTolerance = 0
  References2D = -> [View004]
  Rotation = 0
  ScaleType = 0
  TheoreticalExact = false
  Type = 2
  UnderTolerance = 0
  X = -57.8499
  Y = 23.7618
FEATURE [TechDraw::DrawPage] Page001
  KeepUpdated = true
  NextBalloonIndex = 1
  ProjectionType = 0
  Template = -> Template001
  Views = -> [View004,Dimension019,Dimension020,Dimension021,Dimension022,Dimension023,Dimension024,Dimension025,Dimension026,Dimension027,Dimension028,Dimension029,Dimension030,Dimension031,Dimension032,Dimension033,Dimension034,Dimension035,Dimension036]
